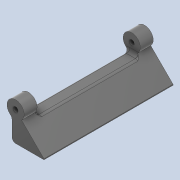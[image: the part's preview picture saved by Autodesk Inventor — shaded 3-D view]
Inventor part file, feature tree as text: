
AUTODESK INVENTOR PART (.ipt)
format: ipt  version: 2020.4 (Build 244396000, 396)  size: 243,200 bytes
history: native  units: mm
features: extrude x3, sketch x3, plane x2, fillet x2, projected_geometry x2, mirror x1
ambient origin geometry x8: Origin, YZ Plane, XZ Plane, XY Plane, X Axis, Y Axis, Z Axis, Center Point
bodies: Solid1 (feature_tree)
feature tree (13):
  extrude  "Extrusion1"  Depth=2.0mm
  plane  "Work Plane1"
  fillet  "Fillet1"  Radius=17.0mm
  extrude  "Extrusion3"  TaperAngle=45.0deg  [1 undecoded]
  extrude  "Extrusion4"  Depth=3.0mm
  fillet  "Fillet2"  Radius=3.0mm
  mirror  "Mirror2"
  plane  "Work Plane2"
  sketch  "Sketch1"  dims[d0=3.0mm d1=2.0mm d2=17.0mm]
  sketch  "Sketch3"  dims[d3=10.0mm d4=45.0deg]
  projected_geometry  "Projected Loop1"
  sketch  "Sketch4"  dims[d5=0.5mm d6=3.0mm d7=3.0mm d8=3.5mm d9=10.0mm d10=3.5mm d11=5.5mm d12=7.5mm d13=0.0mm d18=3.0mm d19=45.0deg d20=1.5mm d21=0.35mm d22=0.0mm d23=12.0mm d24=30.0mm d25=0.0mm d26=22.68928mm d27=8.0mm d28=10.0mm d29=0.0mm d30=2.0mm d31=1.0mm d40=-6.0mm d45=0.5mm d46=0.872665mm d47=0.5mm d48=0.872665mm]
  projected_geometry  "Projected Loop2"
note: 1 required parameter value undecoded (feature->parameter linkage not recoverable at this tier; creation-order binding heuristic only, values carry confidence <= 0.55)
